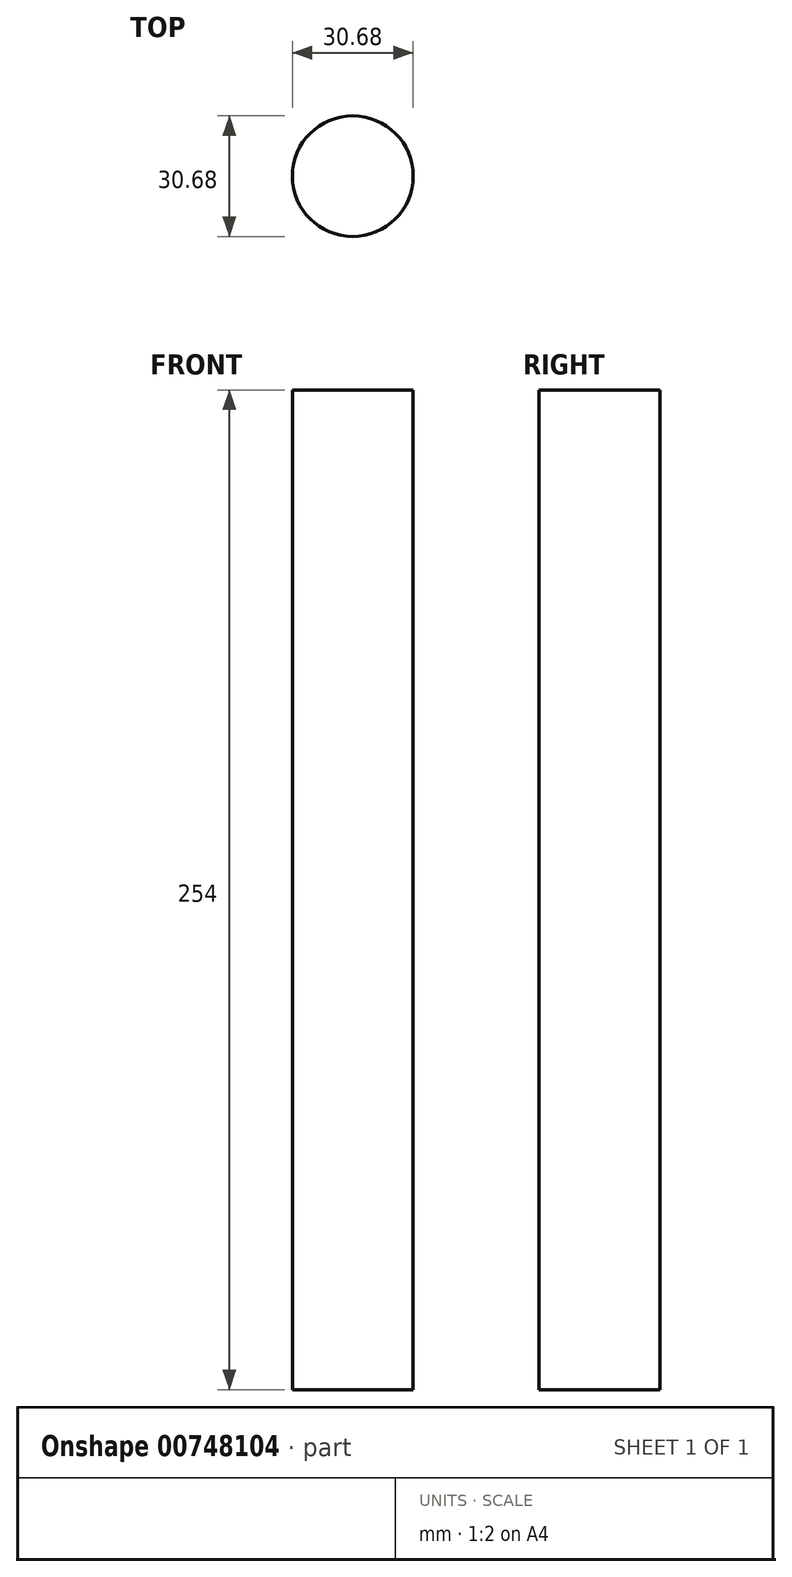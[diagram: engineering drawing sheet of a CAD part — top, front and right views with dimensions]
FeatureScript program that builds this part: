
annotation { "Feature Type Name" : "Feature", "Feature Type Description" : "" }
export const myFeature = defineFeature(function(context is Context, id is Id, definition is map)
    precondition{}
    {
        {
            var Q0;
            Q0=qCreatedBy(makeId("Top.planeOp"),FACE);
            var sketch = newSketch(context, id + "F0", { "sketchPlane" : qUnion([Q0])});
            skCircle(sketch, "E0", {"center": v(0, 0) * mm, "radius": 15.34 * mm});
            skSolve(sketch);
        }
        {
            var Q0;
            Q0=makeQuery(id+"F0.imprint","IMPRINT",FACE,{"disambiguationData":[TD([[makeQuery(id+"F0.imprint","IMPRINT",EDGE,{"derivedFrom":sQuery(id+"F0.wireOp",EDGE,"E0")}),1.0]])]});
            extrude(context, id + "F1", {"entities" : qUnion([Q0]), "depth" : 254 * mm, "offsetDistance" : 25.4 * mm});
        }
    });
